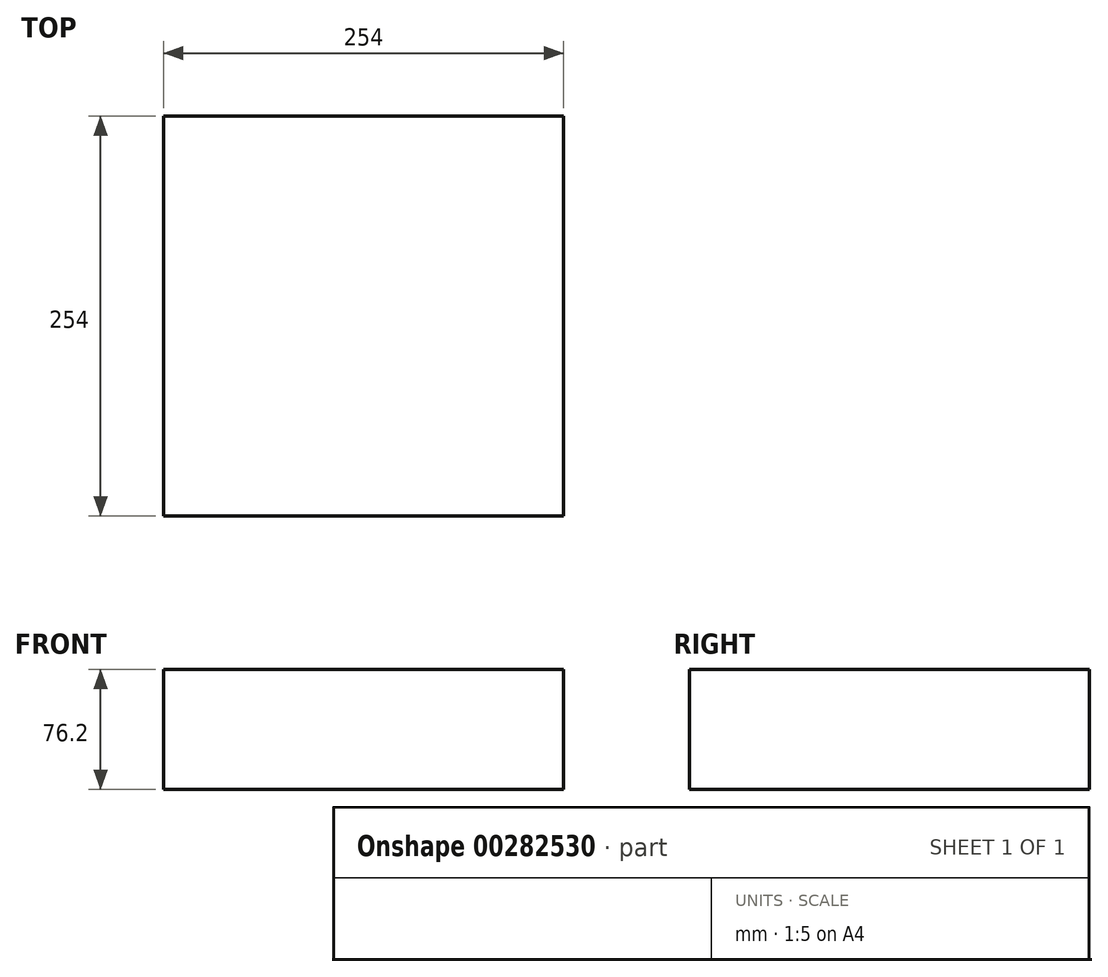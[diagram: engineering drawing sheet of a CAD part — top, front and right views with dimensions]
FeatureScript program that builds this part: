
annotation { "Feature Type Name" : "Feature", "Feature Type Description" : "" }
export const myFeature = defineFeature(function(context is Context, id is Id, definition is map)
    precondition{}
    {
        {
            var Q0;
            Q0=qCreatedBy(makeId("Top.planeOp"),FACE);
            var sketch = newSketch(context, id + "F0", { "sketchPlane" : qUnion([Q0])});
            skLineSegment(sketch, "E0.bottom", {"start": v(127, 127) * mm, "end": v(-127, 127) * mm});
            skLineSegment(sketch, "E0.top", {"start": v(127, -127) * mm, "end": v(-127, -127) * mm});
            skLineSegment(sketch, "E0.left", {"start": v(127, 127) * mm, "end": v(127, -127) * mm});
            skLineSegment(sketch, "E0.right", {"start": v(-127, 127) * mm, "end": v(-127, -127) * mm});
            skPoint(sketch, "E0.middle", {"position": v(0, 0) * mm});
            skSolve(sketch);
        }
        {
            var Q0;
            Q0=qSketchRegion(id+"F0",true);
            extrude(context, id + "F1", {"entities" : qUnion([Q0]), "endBound" : BoundingType.SYMMETRIC, "depth" : 76.2 * mm});
        }
    });
